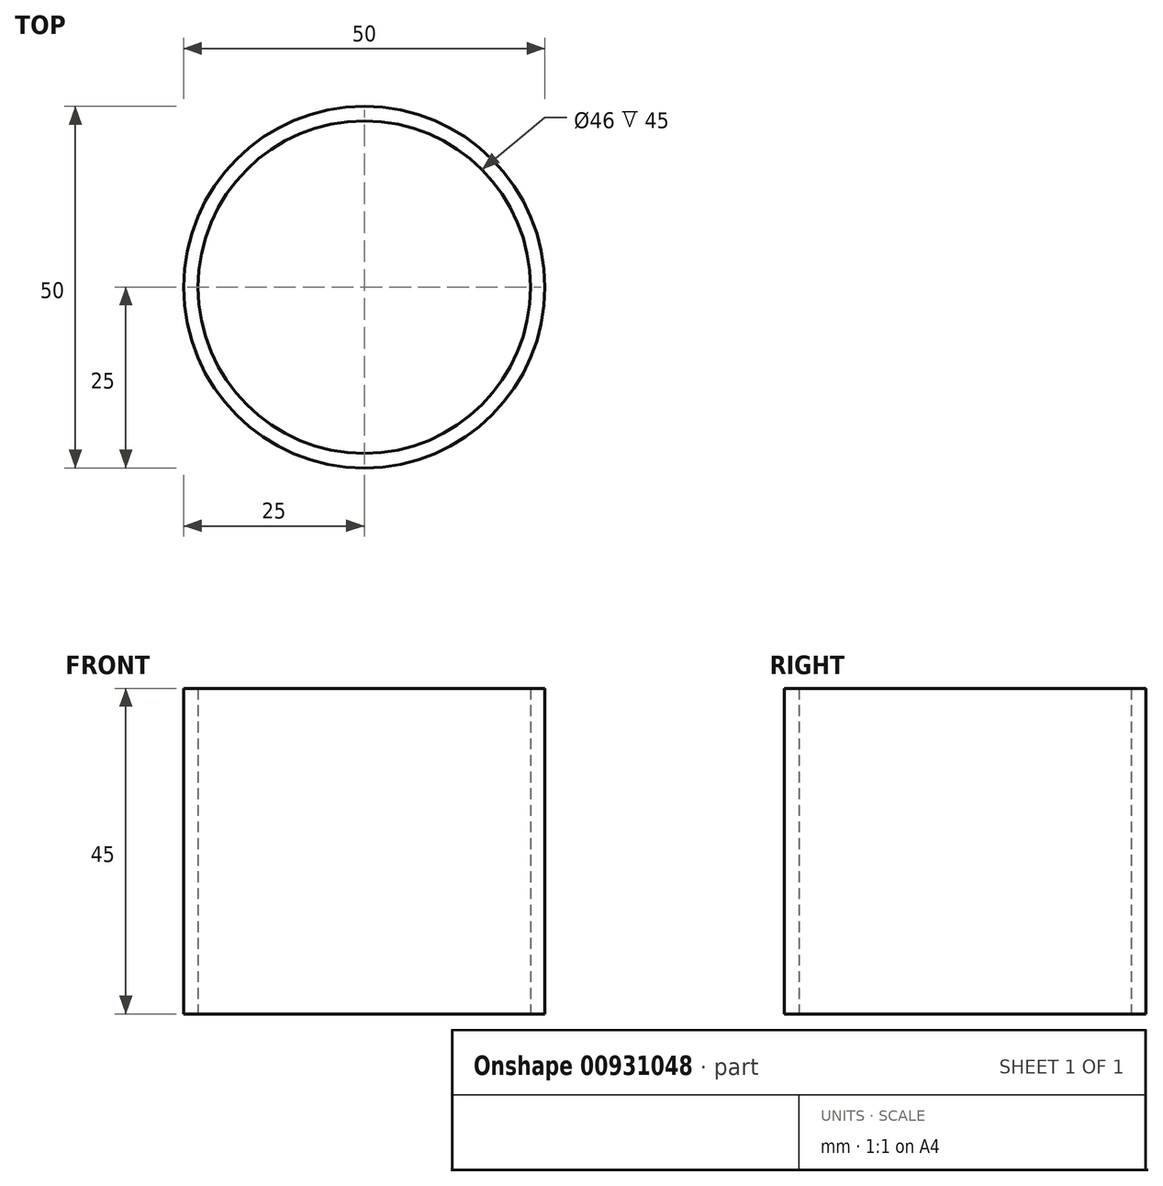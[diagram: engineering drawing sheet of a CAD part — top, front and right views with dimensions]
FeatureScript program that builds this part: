
annotation { "Feature Type Name" : "Feature", "Feature Type Description" : "" }
export const myFeature = defineFeature(function(context is Context, id is Id, definition is map)
    precondition{}
    {
        {
            var Q0;
            Q0=qCreatedBy(makeId("Top.planeOp"),FACE);
            var sketch = newSketch(context, id + "F0", { "sketchPlane" : qUnion([Q0])});
            skCircle(sketch, "E0", {"center": v(0, 0) * mm, "radius": 25 * mm});
            skCircle(sketch, "E1", {"center": v(0, 0) * mm, "radius": 23 * mm});
            skSolve(sketch);
        }
        {
            var Q0;
            Q0=makeQuery(id+"F0.imprint","IMPRINT",FACE,{"disambiguationData":[TD([[makeQuery(id+"F0.imprint","IMPRINT",EDGE,{"derivedFrom":sQuery(id+"F0.wireOp",EDGE,"E0")}),1.0]])]});
            extrude(context, id + "F1", {"entities" : qUnion([Q0]), "depth" : 45 * mm, "offsetDistance" : 25 * mm});
        }
    });
